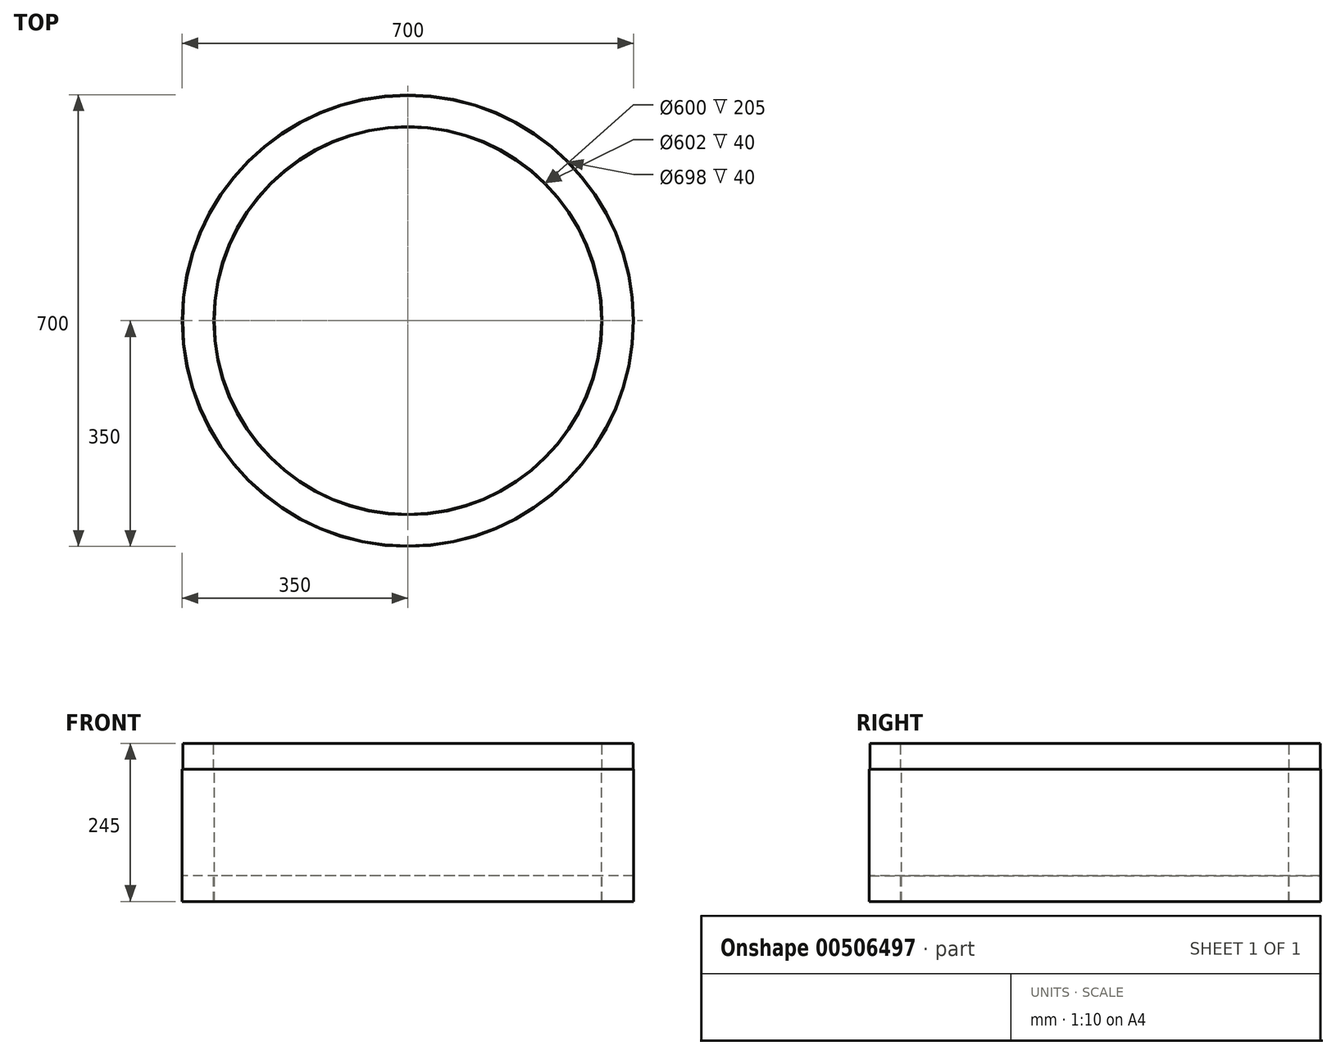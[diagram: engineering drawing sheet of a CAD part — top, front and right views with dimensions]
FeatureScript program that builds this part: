
annotation { "Feature Type Name" : "Feature", "Feature Type Description" : "" }
export const myFeature = defineFeature(function(context is Context, id is Id, definition is map)
    precondition{}
    {
        {
            var Q0;
            Q0=qCreatedBy(makeId("Front.planeOp"),FACE);
            var sketch = newSketch(context, id + "F0", { "sketchPlane" : qUnion([Q0])});
            skLineSegment(sketch, "E0", {"start": v(0, 74.87) * mm, "end": v(0, -73.71) * mm, "construction": true});
            skLineSegment(sketch, "E1", {"start": v(0, 374.84) * mm, "end": v(0, -528.94) * mm, "construction": true});
            skLineSegment(sketch, "E2", {"start": v(-300, -489.75) * mm, "end": v(-300, -284.75) * mm});
            skLineSegment(sketch, "E3", {"start": v(-300, -284.75) * mm, "end": v(-301, -284.75) * mm});
            skLineSegment(sketch, "E4", {"start": v(-301, -284.75) * mm, "end": v(-301, -244.75) * mm});
            skLineSegment(sketch, "E5", {"start": v(-301, -244.75) * mm, "end": v(-349, -244.75) * mm});
            skLineSegment(sketch, "E6", {"start": v(-349, -244.75) * mm, "end": v(-349, -284.75) * mm});
            skLineSegment(sketch, "E7", {"start": v(-349, -284.75) * mm, "end": v(-350, -284.75) * mm});
            skLineSegment(sketch, "E8", {"start": v(-350, -284.75) * mm, "end": v(-350, -489.75) * mm});
            skLineSegment(sketch, "E9", {"start": v(-350, -489.75) * mm, "end": v(-349, -489.75) * mm});
            skLineSegment(sketch, "E10", {"start": v(-349, -489.75) * mm, "end": v(-349, -449.75) * mm});
            skLineSegment(sketch, "E11", {"start": v(-349, -449.75) * mm, "end": v(-301, -449.75) * mm});
            skLineSegment(sketch, "E12", {"start": v(-301, -449.75) * mm, "end": v(-301, -489.75) * mm});
            skLineSegment(sketch, "E13", {"start": v(-301, -489.75) * mm, "end": v(-300, -489.75) * mm});
            skSolve(sketch);
        }
        {
            var Q0;
            Q0=qSketchRegion(id+"F0",true);
            var Q1;
            Q1=sQuery(id+"F0.wireOp",EDGE,"E1");
            revolve(context, id + "F1", {"entities" : qUnion([Q0]), "axis" : qUnion([Q1]), "revolveType" : RevolveType.FULL});
        }
    });
